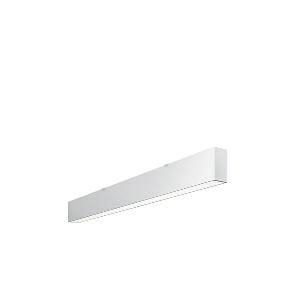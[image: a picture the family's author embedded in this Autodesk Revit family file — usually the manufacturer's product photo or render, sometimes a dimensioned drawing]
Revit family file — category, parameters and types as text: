
# Revit family: dotoo_line_-_dla_2000_840_d_end_00807933_6931
name_source: partatom
category: Lighting Fixtures
units: mm (PartAtom-declared; Revit-internal decimal feet)

## family parameters
Cut with Voids When Loaded = No
Host = Face
Light Source = No
Part Type = Normal
Room Calculation Point = No
Round Connector Dimension = Use Diameter
Shared = No

## types (1)
- DOTOO.line - DLA 2000/840/D END (1 x LED, 1700 lm, 4000K)
    Apparent Load = 16 VA
    Approval mark = CE
    CIE Flux Codes = 67 91 98 100 100
    Color Rendering = 80-89
    Color Temperature = 4000K
    Control Gear = Electronic ballast
    Default Elevation = 1800 mm
    Description = DLA 2000/840/D|Surface-mounted luminaire.|light source: LED|work equipment: Adjustable electronic ballast, digital DALI|connected load: 220-240 V, 50/60 Hz|Power consumption: approx. 16 W|luminous flux: 1700 lm|luminous efficacy: 106 lm/W|light distribution: Direct|colour temperature: Cold white, ca. 4000 K|class of protection: I|technology: Continuously dimmable|mains lead: Connector|glare control: Prism aperture|special features: DALI Load 1x, TouchDIM - dimming via standard switch, Through-wired, up to 18 m on one mains connection, Flicker-free, Suitable as emergency lighting, Mechanical and electrical connection of the individual modules without tools|
    Frequency = 50 Hz
    Height = 110 mm
    Lamp = 1 x LED
    Lamp Light Flux = 1700 lm
    Lamp count = 1
    Length = 1408 mm
    Luminous efficacy = 106 lm/W
    Manufacturer = Waldmann
    ModVariant = No
    Model = 00807933
    Mounting Place = Ceiling
    Mounting Type = Surface mounted
    Number of Poles = 1
    OnlyDefault = Yes
    Power Factor = 1
    Product Name = DOTOO.line - DLA 2000/840/D END
    Product group = Ceiling mounted luminaire
    ProductGroupID = 3
    Protection Class = Protection class I
    Protection Degree = IP 40
    RLX_Detail_Level = 1
    RLX_Emergency_Light_Flux = 0 lm
    RLX_Emergency_Type = 0
    RLX_Emergency_Type_DB = No
    RlxData = <blob elided: 15261 chars, md5=1747de80>
    Socket = socket
    Standby Power = 0 W
    System Light Flux = 1700 lm
    System Power = 16 W
    Type Comments = Product without accessories
    Type Image = 114350000-00807927.jpg
    URL = http://relux.com
    VarID = ---
    Voltage = 230 V
    Voltage Range = 220-240 V
    Weight = 0.00 kg
    Width = 60 mm  [stored 0.19685 ft]

note: [stored X ft] marks values corroborated as IEEE doubles in the binary element streams (Revit-internal decimal feet)

## geometry (parser evidence)
native form markers: Sweep x11
no freeform markers — native parametric forms only
